# Revit family: Furniture_Office-Chairs_Flokk_HAG_SoFi_7500
name_source: partatom
category: Furniture
units: mm (PartAtom-declared; Revit-internal decimal feet)

## family parameters
Always vertical = Yes
Cut with Voids When Loaded = No
OmniClass Number = 23.40.20.14.14.11
OmniClass Title = Chairs
Room Calculation Point = No
Shared = No
Work Plane-Based = No

## types (1)
- HAG SoFi 7500
    AssetType = Movable
    BIMObjectName = Furniture_Office-Chairs_Flokk_HAG_SoFi_7500
    Brand = HAG
    Category = Task chairs
    Collection = HAG SoFi
    Color = Various
    Cost = 0 $
    Default Elevation = 0 mm  [stored 0 ft]
    Description = The HÅG SoFi 7500 is a mesh chair that provides you with the ventilation benefits of a breathable, transparent backrest. HÅG in Balance® technology ensures more subconscious movement. Adjustable seat height and depth, and unique fully functional lumbar support. The seat, lumbar support and headrest can be dressed up in a variety of colours from the HÅG Total Colour Standard and extended textile collections to satisfy individual preferences and achieve the desired style. Available with HÅG SlideBack™ armrests which allow you to move closer to your desk, invite you to sit sideways or use the armrests as elbow support.
    Designer = Frost Produkt AS, Powerdesign AS
and Scandinavian Business Seating Design Team
    DurationUnit = Year
    Features = Adjustable seat height and depth, lumbar support, HÅG SlideBack™ armrests armrests (optional extra), armrest height, armrest width, seat height, seat depth, lumbar support, tilt resistance/HÅG inBalance™, lockable tilt and foot support
    HighestSeatingHeight = 640 mm  [stored 2.09974 ft]
    IfcExportAs = IfcFurnishingElementType
    IfcExportType = CHAIR
    LowestSeatingHeight = 450 mm  [stored 1.47638 ft]
    MainColor = Various
    Manufacturer = Flokk
    ManufacturerName = Flokk
    ManufacturerURL = https://www.flokk.com
    Material = Textile, metal, plastic
    Model = HAG SoFi 7500
    ModelNumber = 7500
    NBSDescription = Office chairs
    NBSReference = 45-35-20/330
    Name = HAG_SoFi_7500
    NominalDepth = 670 mm  [stored 2.19816 ft]
    NominalHeight = 1045 mm  [stored 3.42848 ft]
    NominalLength = 670 mm  [stored 2.19816 ft]
    OfficeChairSecondaryMaterial = Stainless Steel AISI 304
    OfficeChairTertiaryMaterial = Plastic Black
    OffieChairTertiaryMaterial = Plastic Black
    ProductInformation = The HÅG SoFi 7500 is a mesh chair that provides you with the ventilation benefits of a breathable, transparent backrest. HÅG in Balance® technology ensures more subconscious movement. Adjustable seat height and depth, and unique fully functional lumbar support. The seat, lumbar support and headrest can be dressed up in a variety of colours from the HÅG Total Colour Standard and extended textile collections to satisfy individual preferences and achieve the desired style. Available with HÅG SlideBack™ armrests which allow you to move closer to your desk, invite you to sit sideways or use the armrests as elbow support.
    Revision = 4
    SeatingHeight = 497 mm  [stored 1.63058 ft]
    Shape = Sculptured
    ShareRecyclableMaterials = 96%
    ShareRecycledMaterials = 45%
    Size = 670x670x1045/1235mm
    URL = https://store.flokk.com
    Uniclass2 = Pr_40_50_12_57
    Uniclass2015Description = Office chairs
    Uniclass2015Reference = Pr_40_50_12_57
    Version = 2
    VersionDate = 11/11/2022
    WarrantyDurationUnit = Year
    Weight = 22.5 kg

note: [stored X ft] marks values corroborated as IEEE doubles in the binary element streams (Revit-internal decimal feet)

## geometry (parser evidence)
native form markers: Sweep x13
no freeform markers — native parametric forms only
